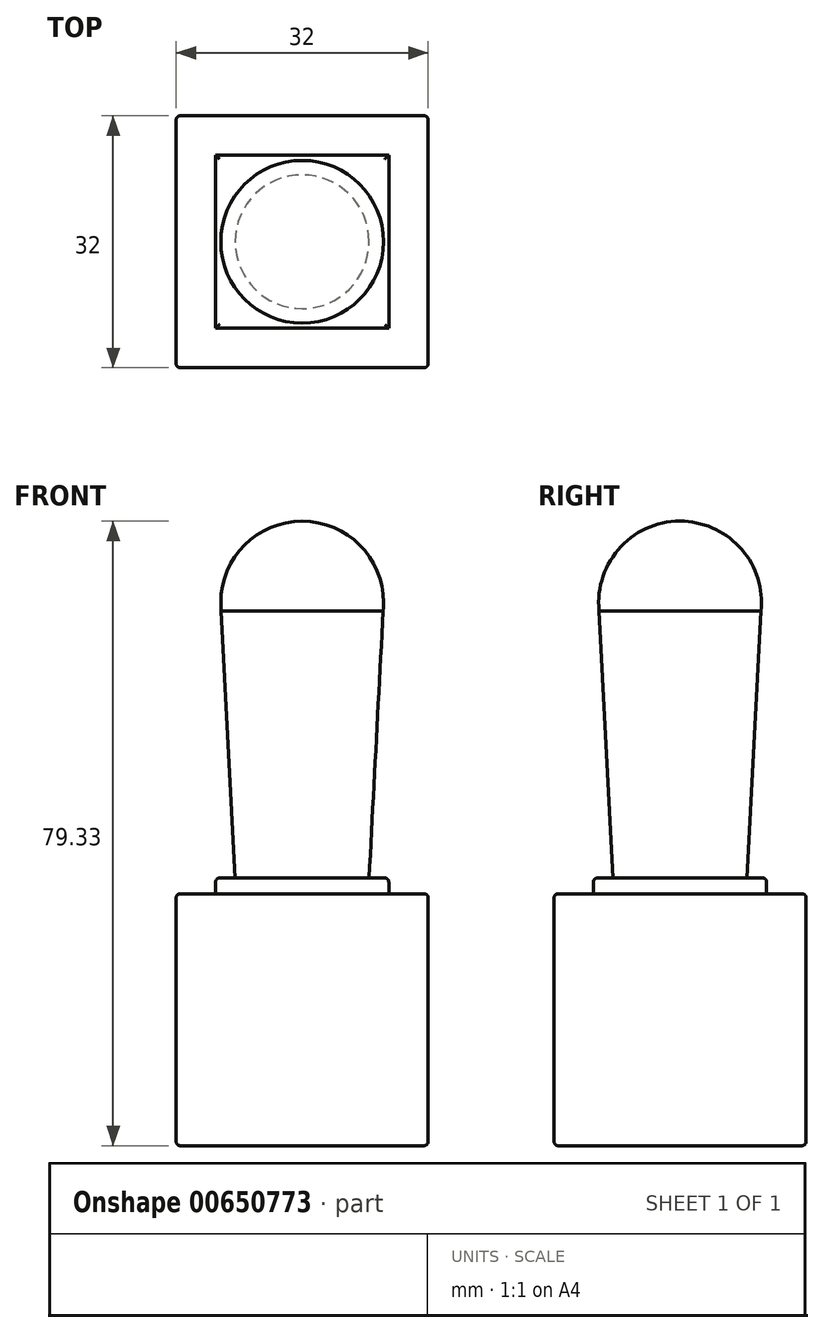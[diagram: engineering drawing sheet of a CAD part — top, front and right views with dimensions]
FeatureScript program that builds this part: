
annotation { "Feature Type Name" : "Feature", "Feature Type Description" : "" }
export const myFeature = defineFeature(function(context is Context, id is Id, definition is map)
    precondition{}
    {
        {
            var Q0;
            Q0=qCreatedBy(makeId("Top.planeOp"),FACE);
            var sketch = newSketch(context, id + "F0", { "sketchPlane" : qUnion([Q0])});
            skLineSegment(sketch, "E0.bottom", {"start": v(-16, 16) * mm, "end": v(16, 16) * mm});
            skLineSegment(sketch, "E0.top", {"start": v(-16, -16) * mm, "end": v(16, -16) * mm});
            skLineSegment(sketch, "E0.left", {"start": v(-16, 16) * mm, "end": v(-16, -16) * mm});
            skLineSegment(sketch, "E0.right", {"start": v(16, 16) * mm, "end": v(16, -16) * mm});
            skPoint(sketch, "E0.middle", {"position": v(0, 0) * mm});
            skSolve(sketch);
        }
        {
            var Q0;
            Q0 = qSketchRegion(id + "F0", true);
            extrude(context, id + "F1", {"entities" : qUnion([Q0]), "depth" : 32 * mm, "offsetDistance" : 25 * mm});
        }
        {
            var Q0;
            Q0=makeQuery(id+"F1.opExtrude","CAP_FACE",FACE,{"disambiguationData":[OSD([sQuery(id+"F0.wireOp",EDGE,"E0.bottom"),sQuery(id+"F0.wireOp",EDGE,"E0.top"),sQuery(id+"F0.wireOp",EDGE,"E0.left"),sQuery(id+"F0.wireOp",EDGE,"E0.right")])],"isStart":false});
            var sketch = newSketch(context, id + "F2", { "sketchPlane" : qUnion([Q0])});
            skLineSegment(sketch, "E1.bottom", {"start": v(11, 11) * mm, "end": v(-11, 11) * mm});
            skLineSegment(sketch, "E1.top", {"start": v(11, -11) * mm, "end": v(-11, -11) * mm});
            skLineSegment(sketch, "E1.left", {"start": v(11, 11) * mm, "end": v(11, -11) * mm});
            skLineSegment(sketch, "E1.right", {"start": v(-11, 11) * mm, "end": v(-11, -11) * mm});
            skPoint(sketch, "E1.middle", {"position": v(0, 0) * mm});
            skSolve(sketch);
        }
        {
            var Q0;
            Q0=makeQuery(id+"F2.imprint","IMPRINT",FACE,{"disambiguationData":[TD([[makeQuery(id+"F2.imprint","IMPRINT",EDGE,{"derivedFrom":sQuery(id+"F2.wireOp",EDGE,"E1.bottom")}),1.0]])]});
            extrude(context, id + "F3", {"entities" : qUnion([Q0]), "operationType" : NewBodyOperationType.ADD, "depth" : 2 * mm, "offsetDistance" : 25 * mm});
        }
        {
            var Q0;
            Q0=makeQuery(id+"F3.opExtrude","CAP_FACE",FACE,{"disambiguationData":[OSD([sQuery(id+"F2.wireOp",EDGE,"E1.bottom"),sQuery(id+"F2.wireOp",EDGE,"E1.top"),sQuery(id+"F2.wireOp",EDGE,"E1.left"),sQuery(id+"F2.wireOp",EDGE,"E1.right")])],"isStart":false});
            var sketch = newSketch(context, id + "F4", { "sketchPlane" : qUnion([Q0])});
            skCircle(sketch, "E2", {"center": v(0, 0) * mm, "radius": 8.5 * mm});
            skSolve(sketch);
        }
        {
            var Q0;
            Q0=makeQuery(id+"F4.imprint","IMPRINT",FACE,{"disambiguationData":[TD([[makeQuery(id+"F4.imprint","IMPRINT",EDGE,{"derivedFrom":sQuery(id+"F4.wireOp",EDGE,"E2")}),1.0]])]});
            extrude(context, id + "F5", {"entities" : qUnion([Q0]), "operationType" : NewBodyOperationType.ADD, "depth" : 35 * mm, "offsetDistance" : 25 * mm, "hasDraft" : true, "draftAngle" : 3 * degree});
        }
        {
            var Q0;
            Q0=makeQuery(id+"F5.opExtrude","CAP_FACE",FACE,{"disambiguationData":[OSD([sQuery(id+"F4.wireOp",EDGE,"E2")])],"isStart":false});
            var sketch = newSketch(context, id + "F6", { "sketchPlane" : qUnion([Q0])});
            skLineSegment(sketch, "E3", {"start": v(-10.33, 0) * mm, "end": v(0, 0) * mm});
            skLineSegment(sketch, "E4", {"start": v(0, 0) * mm, "end": v(10.33, 0) * mm});
            skSolve(sketch);
        }
        {
            var Q0;
            {var subQ0=sQuery(id+"F6.wireOp",EDGE,"E3");Q0=makeQuery(id+"F6.imprint","IMPRINT",FACE,{"disambiguationData":[TD([[makeQuery(id+"F6.imprint","IMPRINT",EDGE,{"derivedFrom":subQ0}),1.0]])]});}
            var Q1;
            Q1=sQuery(id+"F6.wireOp",EDGE,"E3");
            revolve(context, id + "F7", {"operationType" : NewBodyOperationType.ADD, "entities" : qUnion([Q0]), "axis" : qUnion([Q1]), "revolveType" : RevolveType.FULL});
        }
        {
            var Q0;
            Q0=makeQuery(id+"F3.opExtrude","CAP_EDGE",EDGE,{"disambiguationData":[OSD([sQuery(id+"F2.wireOp",EDGE,"E1.top")])],"isStart":false});
            var Q1;
            Q1=makeQuery(id+"F3.opExtrude","CAP_EDGE",EDGE,{"disambiguationData":[OSD([sQuery(id+"F2.wireOp",EDGE,"E1.left")])],"isStart":false});
            var Q2;
            Q2=makeQuery(id+"F3.opExtrude","CAP_EDGE",EDGE,{"disambiguationData":[OSD([sQuery(id+"F2.wireOp",EDGE,"E1.left")])],"isStart":true});
            var Q3;
            Q3=makeQuery(id+"F3.opExtrude","CAP_EDGE",EDGE,{"disambiguationData":[OSD([sQuery(id+"F2.wireOp",EDGE,"E1.top")])],"isStart":true});
            var Q4;
            Q4=makeQuery(id+"F1.opExtrude","CAP_EDGE",EDGE,{"disambiguationData":[OSD([sQuery(id+"F0.wireOp",EDGE,"E0.bottom")])],"isStart":true});
            var Q5;
            Q5=makeQuery(id+"F3.opExtrude","CAP_EDGE",EDGE,{"disambiguationData":[OSD([sQuery(id+"F2.wireOp",EDGE,"E1.bottom")])],"isStart":true});
            var Q6;
            Q6=makeQuery(id+"F3.opExtrude","CAP_EDGE",EDGE,{"disambiguationData":[OSD([sQuery(id+"F2.wireOp",EDGE,"E1.bottom")])],"isStart":false});
            var Q7;
            Q7=makeQuery(id+"F3.opExtrude","CAP_EDGE",EDGE,{"disambiguationData":[OSD([sQuery(id+"F2.wireOp",EDGE,"E1.right")])],"isStart":true});
            var Q8;
            Q8=makeQuery(id+"F3.opExtrude","CAP_EDGE",EDGE,{"disambiguationData":[OSD([sQuery(id+"F2.wireOp",EDGE,"E1.right")])],"isStart":false});
            var Q9;
            Q9=makeQuery(id+"F5.opExtrude","CAP_EDGE",EDGE,{"disambiguationData":[OSD([sQuery(id+"F4.wireOp",EDGE,"E2")])],"isStart":true});
            fillet(context, id + "F8", {"entities" : qUnion([Q0, Q1, Q2, Q3, Q4, Q5, Q6, Q7, Q8, Q9]), "radius" : 0.5 * mm, "tangentPropagation" : true, "allowEdgeOverflow" : false});
        }
        {
            var Q0;
            Q0=makeQuery(id+"F1.opExtrude","CAP_EDGE",EDGE,{"disambiguationData":[OSD([sQuery(id+"F0.wireOp",EDGE,"E0.top")])],"isStart":false});
            var Q1;
            Q1=makeQuery(id+"F1.opExtrude","CAP_EDGE",EDGE,{"disambiguationData":[OSD([sQuery(id+"F0.wireOp",EDGE,"E0.right")])],"isStart":false});
            var Q2;
            Q2=makeQuery(id+"F1.opExtrude","SWEPT_EDGE",EDGE,{"disambiguationData":[OSD([sQuery(id+"F0.wireOp",EDGE,"E0.top"),sQuery(id+"F0.wireOp",EDGE,"E0.right")])]});
            var Q3;
            Q3=makeQuery(id+"F1.opExtrude","SWEPT_EDGE",EDGE,{"disambiguationData":[OSD([sQuery(id+"F0.wireOp",EDGE,"E0.bottom"),sQuery(id+"F0.wireOp",EDGE,"E0.right")])]});
            var Q4;
            Q4=makeQuery(id+"F1.opExtrude","SWEPT_EDGE",EDGE,{"disambiguationData":[OSD([sQuery(id+"F0.wireOp",EDGE,"E0.top"),sQuery(id+"F0.wireOp",EDGE,"E0.left")])]});
            var Q5;
            Q5=makeQuery(id+"F1.opExtrude","CAP_EDGE",EDGE,{"disambiguationData":[OSD([sQuery(id+"F0.wireOp",EDGE,"E0.top")])],"isStart":true});
            var Q6;
            Q6=makeQuery(id+"F1.opExtrude","CAP_EDGE",EDGE,{"disambiguationData":[OSD([sQuery(id+"F0.wireOp",EDGE,"E0.right")])],"isStart":true});
            var Q7;
            Q7=makeQuery(id+"F1.opExtrude","CAP_EDGE",EDGE,{"disambiguationData":[OSD([sQuery(id+"F0.wireOp",EDGE,"E0.bottom")])],"isStart":false});
            var Q8;
            Q8=makeQuery(id+"F1.opExtrude","CAP_EDGE",EDGE,{"disambiguationData":[OSD([sQuery(id+"F0.wireOp",EDGE,"E0.left")])],"isStart":false});
            var Q9;
            Q9=makeQuery(id+"F1.opExtrude","CAP_EDGE",EDGE,{"disambiguationData":[OSD([sQuery(id+"F0.wireOp",EDGE,"E0.left")])],"isStart":true});
            fillet(context, id + "F9", {"entities" : qUnion([Q0, Q1, Q2, Q3, Q4, Q5, Q6, Q7, Q8, Q9]), "radius" : 0.5 * mm, "tangentPropagation" : true, "allowEdgeOverflow" : false});
        }
    });
